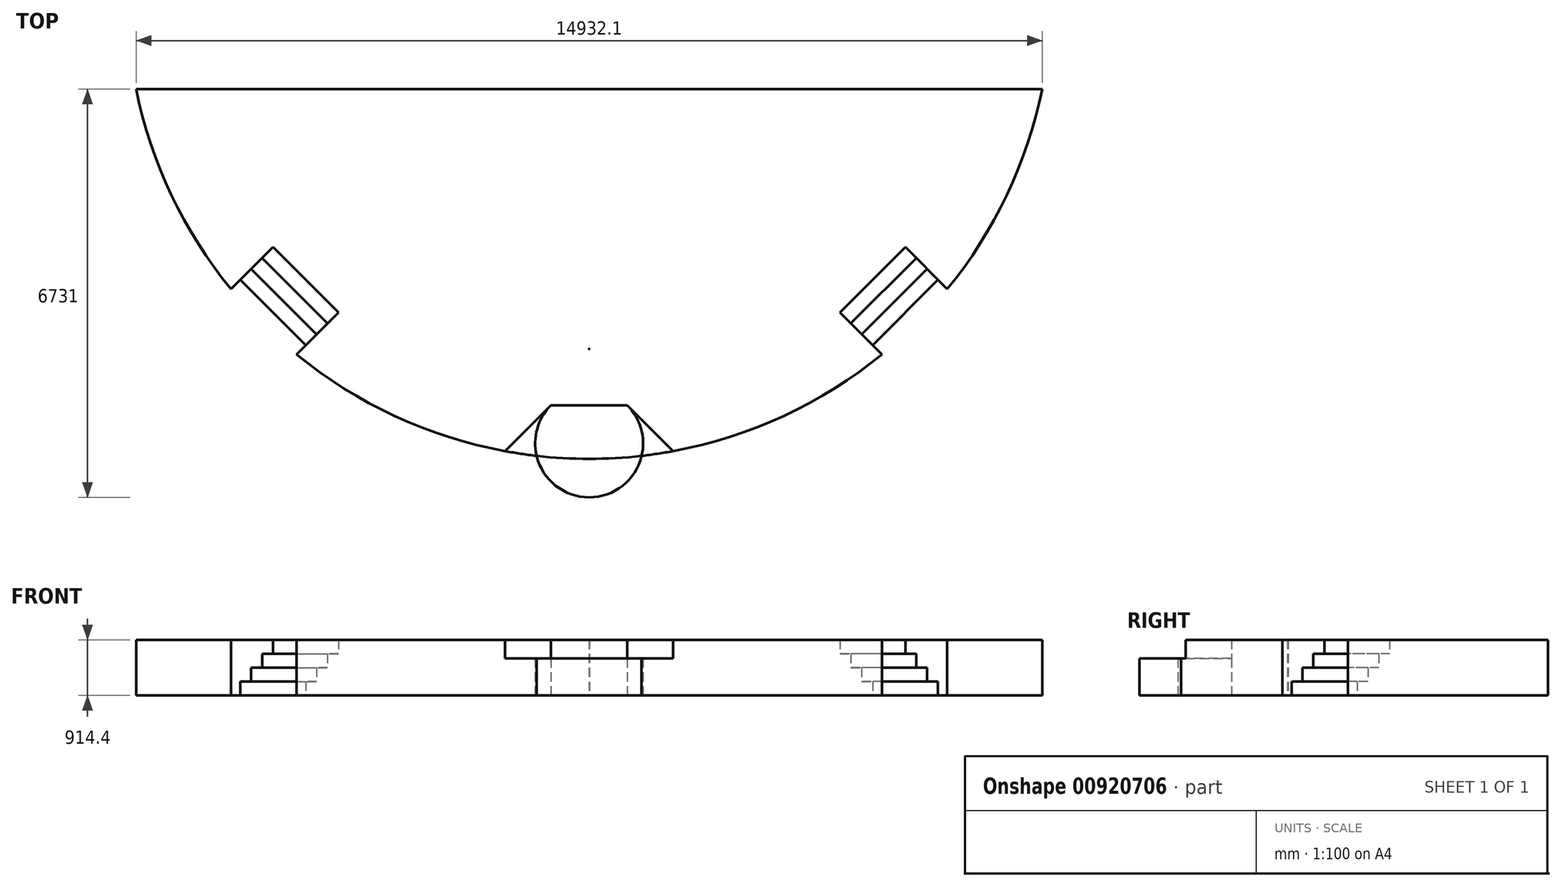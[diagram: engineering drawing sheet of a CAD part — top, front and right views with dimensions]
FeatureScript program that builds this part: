
annotation { "Feature Type Name" : "Feature", "Feature Type Description" : "" }
export const myFeature = defineFeature(function(context is Context, id is Id, definition is map)
    precondition{}
    {
        {
            var Q0;
            Q0=qCreatedBy(makeId("Top.planeOp"),FACE);
            var sketch = newSketch(context, id + "F0", { "sketchPlane" : qUnion([Q0])});
            skArc(sketch, "E0", {"start": v(7466.04, -1524) * mm, "mid": v(0, -7620) * mm, "end": v(-7466.04, -1524) * mm});
            skLineSegment(sketch, "E1", {"start": v(-7466.04, -1524) * mm, "end": v(7466.04, -1524) * mm});
            skLineSegment(sketch, "E2", {"start": v(0, 0) * mm, "end": v(0, -7366) * mm, "construction": true});
            skCircle(sketch, "E3", {"center": v(0, -7366) * mm, "radius": 889 * mm});
            skLineSegment(sketch, "E4", {"start": v(1384.42, -7493.18) * mm, "end": v(628.62, -6737.38) * mm});
            skLineSegment(sketch, "E5", {"start": v(-1384.42, -7493.18) * mm, "end": v(-628.62, -6737.38) * mm});
            skLineSegment(sketch, "E6", {"start": v(-1384.42, -7493.18) * mm, "end": v(1384.42, -7493.18) * mm, "construction": true});
            skLineSegment(sketch, "E7.0", {"start": v(-5208.55, -4130.92) * mm, "end": v(-5926.97, -4849.34) * mm});
            skLineSegment(sketch, "E8.0", {"start": v(0, 0) * mm, "end": v(-5388.15, -5388.15) * mm, "construction": true});
            skLineSegment(sketch, "E9.0", {"start": v(-4130.92, -5208.55) * mm, "end": v(-4849.34, -5926.97) * mm});
            skLineSegment(sketch, "E10", {"start": v(-5926.97, -4849.34) * mm, "end": v(-4849.34, -5926.97) * mm, "construction": true});
            skLineSegment(sketch, "E11", {"start": v(-5747.36, -4669.73) * mm, "end": v(-4669.73, -5747.36) * mm});
            skLineSegment(sketch, "E12", {"start": v(-5567.76, -4490.13) * mm, "end": v(-4490.13, -5567.76) * mm});
            skLineSegment(sketch, "E13", {"start": v(-5388.15, -4310.52) * mm, "end": v(-4310.52, -5388.15) * mm});
            skLineSegment(sketch, "E14", {"start": v(-5208.55, -4130.92) * mm, "end": v(-4130.92, -5208.55) * mm});
            skLineSegment(sketch, "E15.MirrorCS", {"start": v(5926.97, -4849.34) * mm, "end": v(4849.34, -5926.97) * mm, "construction": true});
            skLineSegment(sketch, "E16.MirrorCS", {"start": v(0, 0) * mm, "end": v(5388.15, -5388.15) * mm, "construction": true});
            skLineSegment(sketch, "E17.MirrorCS", {"start": v(5747.36, -4669.73) * mm, "end": v(4669.73, -5747.36) * mm});
            skLineSegment(sketch, "E18.MirrorCS", {"start": v(5567.76, -4490.13) * mm, "end": v(4490.13, -5567.76) * mm});
            skLineSegment(sketch, "E19.MirrorCS", {"start": v(5388.15, -4310.52) * mm, "end": v(4310.52, -5388.15) * mm});
            skLineSegment(sketch, "E20.MirrorCS", {"start": v(5208.55, -4130.92) * mm, "end": v(4130.92, -5208.55) * mm});
            skLineSegment(sketch, "E21.MirrorCS", {"start": v(4130.92, -5208.55) * mm, "end": v(4849.34, -5926.97) * mm});
            skLineSegment(sketch, "E22.MirrorCS", {"start": v(5208.55, -4130.92) * mm, "end": v(5926.97, -4849.34) * mm});
            skCircle(sketch, "E23", {"center": v(0, -5809.04) * mm, "radius": 4.76 * mm});
            skLineSegment(sketch, "E24", {"start": v(-609.6, -6934.2) * mm, "end": v(609.6, -6934.2) * mm, "construction": true});
            skLineSegment(sketch, "E25", {"start": v(-457.2, -7162.8) * mm, "end": v(457.2, -7162.8) * mm, "construction": true});
            skLineSegment(sketch, "E26", {"start": v(0, -7162.8) * mm, "end": v(0, -6934.2) * mm, "construction": true});
            skLineSegment(sketch, "E27", {"start": v(0, -7162.8) * mm, "end": v(0, -7391.4) * mm, "construction": true});
            skLineSegment(sketch, "E28", {"start": v(-304.8, -7391.4) * mm, "end": v(304.8, -7391.4) * mm, "construction": true});
            skPoint(sketch, "E29", {"position": v(-304.8, -6934.2) * mm});
            skPoint(sketch, "E30", {"position": v(304.8, -6934.2) * mm});
            skPoint(sketch, "E31", {"position": v(-152.4, -7162.8) * mm});
            skPoint(sketch, "E32", {"position": v(152.4, -7162.8) * mm});
            skCircle(sketch, "E33", {"center": v(-609.6, -6934.2) * mm, "radius": 25.4 * mm});
            skCircle(sketch, "E34", {"center": v(609.6, -6934.2) * mm, "radius": 25.4 * mm});
            skCircle(sketch, "E35", {"center": v(-457.2, -7162.8) * mm, "radius": 25.4 * mm});
            skCircle(sketch, "E36", {"center": v(457.2, -7162.8) * mm, "radius": 25.4 * mm});
            skCircle(sketch, "E37", {"center": v(-304.8, -7391.4) * mm, "radius": 25.4 * mm});
            skCircle(sketch, "E38", {"center": v(304.8, -7391.4) * mm, "radius": 25.4 * mm});
            skCircle(sketch, "E39", {"center": v(0, -7391.4) * mm, "radius": 25.4 * mm});
            skCircle(sketch, "E40", {"center": v(0, -6934.2) * mm, "radius": 25.4 * mm});
            skCircle(sketch, "E41", {"center": v(-304.8, -6934.2) * mm, "radius": 25.4 * mm});
            skCircle(sketch, "E42", {"center": v(304.8, -6934.2) * mm, "radius": 25.4 * mm});
            skCircle(sketch, "E43", {"center": v(-152.4, -7162.8) * mm, "radius": 25.4 * mm});
            skCircle(sketch, "E44", {"center": v(152.4, -7162.8) * mm, "radius": 25.4 * mm});
            skLineSegment(sketch, "E45", {"start": v(0, -7391.4) * mm, "end": v(0, -7620) * mm, "construction": true});
            skLineSegment(sketch, "E46", {"start": v(0, -6477) * mm, "end": v(669.53, -6477) * mm, "construction": true});
            skLineSegment(sketch, "E47", {"start": v(-628.62, -6737.38) * mm, "end": v(628.62, -6737.38) * mm});
            skSolve(sketch);
        }
        {
            var Q0;
            {var subQ22=sQuery(id+"F0.wireOp",EDGE,"E1");Q0=makeQuery(id+"F0.imprint","IMPRINT",FACE,{"disambiguationData":[TD([[makeQuery(id+"F0.imprint","IMPRINT",EDGE,{"derivedFrom":subQ22}),-1.0]])]});}
            var Q1;
            {var subQ0=sQuery(id+"F0.wireOp",EDGE,"E47");Q1=makeQuery(id+"F0.imprint","IMPRINT",FACE,{"disambiguationData":[TD([[makeQuery(id+"F0.imprint","IMPRINT",EDGE,{"derivedFrom":subQ0}),1.0]])]});}
            extrude(context, id + "F1", {"entities" : qUnion([Q0, Q1]), "depth" : 914.4 * mm, "offsetDistance" : 25.4 * mm});
        }
        {
            var Q0;
            {var subQ0=sQuery(id+"F0.wireOp",EDGE,"E5");Q0=makeQuery(id+"F0.imprint","IMPRINT",FACE,{"disambiguationData":[TD([[makeQuery(id+"F0.imprint","IMPRINT",EDGE,{"derivedFrom":subQ0}),-1.0]])]});}
            var Q1;
            {var subQ0=sQuery(id+"F0.wireOp",EDGE,"E4");Q1=makeQuery(id+"F0.imprint","IMPRINT",FACE,{"disambiguationData":[TD([[makeQuery(id+"F0.imprint","IMPRINT",EDGE,{"derivedFrom":subQ0}),1.0]])]});}
            var Q2;
            {var subQ9=sQuery(id+"F0.wireOp",EDGE,"E3");var subQ10=sQuery(id+"F0.wireOp",EDGE,"E0");var subQ11=makeQuery(id+"F0.imprint","INTERSECT",VERTEX,{"disambiguationData":[OD(0.0)],"derivedFrom":[subQ10,subQ9]});Q2=makeQuery(id+"F0.imprint","IMPRINT",FACE,{"disambiguationData":[TD([[makeQuery(id+"F0.imprint","IMPRINT",EDGE,{"disambiguationData":[TD([[subQ11,-1.0]])],"derivedFrom":subQ10}),-1.0]])]});}
            var Q3;
            {var subQ13=sQuery(id+"F0.wireOp",EDGE,"gZVcGr80-SSea-ewgu-iMrP-pQ58HQi7oUkL");var subQ20=sQuery(id+"F0.wireOp",EDGE,"766fbab4-9368-4186-8d45-a14387564036.0");var subQ21=makeQuery(id+"F0.imprint","INTERSECT",VERTEX,{"derivedFrom":[subQ20,subQ13]});Q3=makeQuery(id+"F0.imprint","IMPRINT",FACE,{"disambiguationData":[TD([[makeQuery(id+"F0.imprint","IMPRINT",EDGE,{"disambiguationData":[TD([[subQ21,-1.0]])],"derivedFrom":subQ20}),-1.0]])]});}
            extrude(context, id + "F2", {"entities" : qUnion([Q0, Q1, Q2, Q3]), "operationType" : NewBodyOperationType.ADD, "depth" : 609.6 * mm, "offsetDistance" : 25.4 * mm});
        }
        {
            var Q0;
            {var subQ2=sQuery(id+"F0.wireOp",EDGE,"E13");Q0=makeQuery(id+"F0.imprint","IMPRINT",FACE,{"disambiguationData":[TD([[makeQuery(id+"F0.imprint","IMPRINT",EDGE,{"derivedFrom":subQ2}),1.0]])]});}
            var Q1;
            {var subQ0=sQuery(id+"F0.wireOp",EDGE,"E19.MirrorCS");Q1=makeQuery(id+"F0.imprint","IMPRINT",FACE,{"disambiguationData":[TD([[makeQuery(id+"F0.imprint","IMPRINT",EDGE,{"derivedFrom":subQ0}),-1.0]])]});}
            extrude(context, id + "F3", {"entities" : qUnion([Q0, Q1]), "operationType" : NewBodyOperationType.ADD, "depth" : 685.8 * mm, "offsetDistance" : 25.4 * mm});
        }
        {
            var Q0;
            {var subQ0=sQuery(id+"F0.wireOp",EDGE,"E12");Q0=makeQuery(id+"F0.imprint","IMPRINT",FACE,{"disambiguationData":[TD([[makeQuery(id+"F0.imprint","IMPRINT",EDGE,{"derivedFrom":subQ0}),1.0]])]});}
            var Q1;
            {var subQ0=sQuery(id+"F0.wireOp",EDGE,"E18.MirrorCS");Q1=makeQuery(id+"F0.imprint","IMPRINT",FACE,{"disambiguationData":[TD([[makeQuery(id+"F0.imprint","IMPRINT",EDGE,{"derivedFrom":subQ0}),-1.0]])]});}
            extrude(context, id + "F4", {"entities" : qUnion([Q0, Q1]), "operationType" : NewBodyOperationType.ADD, "depth" : 457.2 * mm, "offsetDistance" : 25.4 * mm});
        }
        {
            var Q0;
            {var subQ0=sQuery(id+"F0.wireOp",EDGE,"E11");Q0=makeQuery(id+"F0.imprint","IMPRINT",FACE,{"disambiguationData":[TD([[makeQuery(id+"F0.imprint","IMPRINT",EDGE,{"derivedFrom":subQ0}),1.0]])]});}
            var Q1;
            {var subQ0=sQuery(id+"F0.wireOp",EDGE,"E17.MirrorCS");Q1=makeQuery(id+"F0.imprint","IMPRINT",FACE,{"disambiguationData":[TD([[makeQuery(id+"F0.imprint","IMPRINT",EDGE,{"derivedFrom":subQ0}),-1.0]])]});}
            extrude(context, id + "F5", {"entities" : qUnion([Q0, Q1]), "operationType" : NewBodyOperationType.ADD, "depth" : 228.6 * mm, "offsetDistance" : 25.4 * mm});
        }
    });
